# Revit family: Electronics_Video-Decoders_Biamp_Tesira_TesiraLUX_OH-1__
name_source: partatom
category: Communication Devices
units: mm (PartAtom-declared; Revit-internal decimal feet)

## family parameters
Cut with Voids When Loaded = No
Host = Face
Maintain Annotation Orientation = No
OmniClass Number = 23.85.10.11.11
OmniClass Title = Sound and Signal Devices
Part Type = Normal
Room Calculation Point = No
Round Connector Dimension = Use Diameter
Shared = No

## types (1)
- OH-1
    A/D - D/A Converters = 24-bit
    Altitude = 0-6,600 ft (0-2000m) MSL
    Apparent Load = 60 VA
    Chroma Subsampling = 4:4:4, 4:2:2, 4:2:0
    Color Depth = 8-bit, 10-bit, 12-bit, 16-bit
    Color Formats = Color Formats
    Colorspace = Up to Rec. 2020
    Compliance = FCC Part 15B (USA); UL and C-UL (USA and Canada); CE Marked (Europe); RoHS Directive (Europe)
    Connector Description = 100 - 240V 50/60Hz
    Control Connection = RJ-45 with Ethernet cable (Cat 5e and above)
    Cross Talk = channel to channel at 1kHz: < -95dB
    Current = 1 A
    Default Elevation = 48 "
    Depth = 10.4 "
    Description = TesiraLUX™ OH-1 AVB Video Decoder
    Dynamic Range = 20Hz~20kHz, 0dB: > 110dB
    Frequency Response = +0.25 dB/-0.5 dB 20Hz~20kHz at +4dBu
    HDMI Audio Formats = 8ch PCM
    Height = 1.75 "
    Housing Material = Biamp - Metal - Silver
    Humidity = 0-95% relative humidity (non-condensing)
    LED Driver = 5V/10mA per output
    Logic Input Trigger = Contact Closure or 5V TTL
    Logic Output Type = Open Collector; Sink 40V/300mA per output
    Manufacturer = Biamp
    Maximum Output = +24dBu
    Media Connections = 1Gb: RJ-45 twisted-pair Ethernet (Cat 5e and above); 10Gb: 10G fiber SFP+
    Model = TesiraLUX OH-1
    No mount = No mount
    Number of Poles = 1
    Output Impedance = 200 ohm (balanced)
    Physical Interface = HDMI
    Power Factor = 1
    Product Documentation Link = https://downloads.biamp.com
    Product Page URL = https://www.biamp.com
    Product data url = https://www.bimobject.com
    RMK-1 = RMK-1
    RMK-2 = RMK-2
    RS-232 = 115200/8-N-1
    Sampling Rate = 48kHz
    Selectable Full Scale Output Levels = +24dBu, +18dBu, +12dBu, +6dBu, 0dBu, -31dBu
    Supported Resolutions = Up to 4K60
    THD+N = 20Hz~20kHz: < 0.0035%
    Temperature Range = 32 - 104° F (0 - 40° C)
    URL = https://www.biamp.com
    UTMK-1 = UTMK-1
    Voltage = 120 V
    Weight = 4.00 lbf
    Width = 8.5 "

## geometry (parser evidence)
native form markers: Sweep x15
no freeform markers — native parametric forms only
